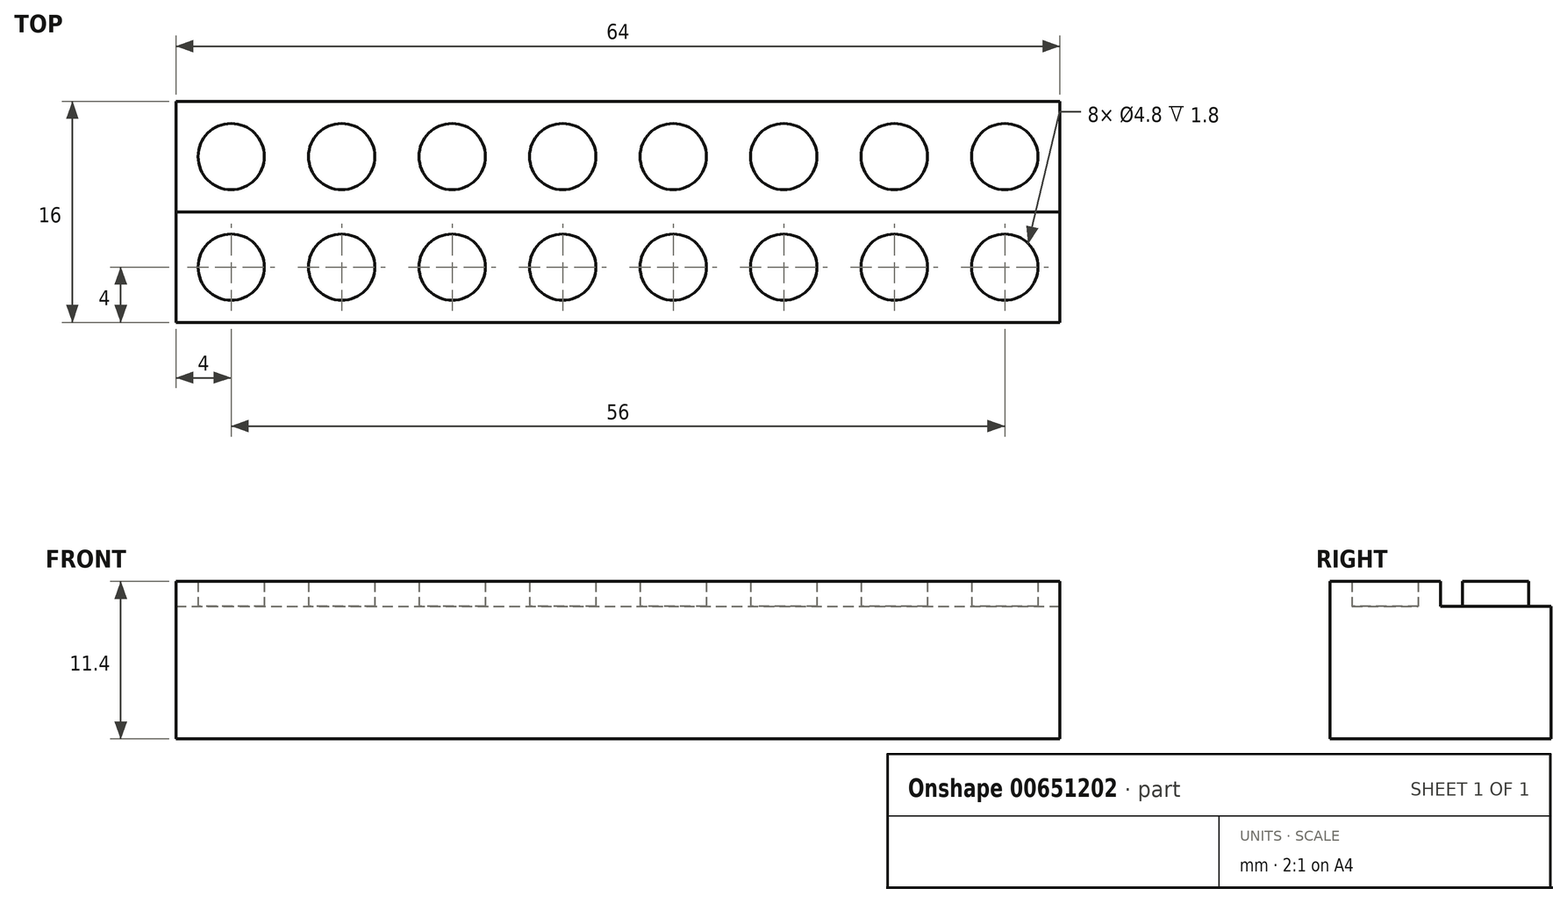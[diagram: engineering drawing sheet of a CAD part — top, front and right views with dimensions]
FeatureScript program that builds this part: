
annotation { "Feature Type Name" : "Feature", "Feature Type Description" : "" }
export const myFeature = defineFeature(function(context is Context, id is Id, definition is map)
    precondition{}
    {
        {
            var Q0;
            Q0=qCreatedBy(makeId("Top.planeOp"),FACE);
            var sketch = newSketch(context, id + "F0", { "sketchPlane" : qUnion([Q0])});
            skLineSegment(sketch, "E0.bottom", {"start": v(0, 0) * mm, "end": v(-64, 0) * mm});
            skLineSegment(sketch, "E0.top", {"start": v(0, 16) * mm, "end": v(-64, 16) * mm});
            skLineSegment(sketch, "E0.left", {"start": v(0, 0) * mm, "end": v(0, 16) * mm});
            skLineSegment(sketch, "E0.right", {"start": v(-64, 0) * mm, "end": v(-64, 16) * mm});
            skSolve(sketch);
        }
        {
            var Q0;
            Q0=makeQuery(id+"F0.imprint","IMPRINT",FACE,{"disambiguationData":[TD([[makeQuery(id+"F0.imprint","IMPRINT",EDGE,{"derivedFrom":sQuery(id+"F0.wireOp",EDGE,"E0.bottom")}),-1.0]])]});
            extrude(context, id + "F1", {"entities" : qUnion([Q0]), "depth" : 9.6 * mm, "offsetDistance" : 25.4 * mm});
        }
        {
            var Q0;
            Q0=makeQuery(id+"F1.opExtrude","CAP_FACE",FACE,{"disambiguationData":[OSD([sQuery(id+"F0.wireOp",EDGE,"E0.bottom"),sQuery(id+"F0.wireOp",EDGE,"E0.top"),sQuery(id+"F0.wireOp",EDGE,"E0.left"),sQuery(id+"F0.wireOp",EDGE,"E0.right")])],"isStart":false});
            var sketch = newSketch(context, id + "F2", { "sketchPlane" : qUnion([Q0])});
            skLineSegment(sketch, "E1", {"start": v(-64, 8) * mm, "end": v(0, 8) * mm});
            skLineSegment(sketch, "E2", {"start": v(-32, 16) * mm, "end": v(-32, 0) * mm});
            skLineSegment(sketch, "E3", {"start": v(-56, 16) * mm, "end": v(-56, 0) * mm});
            skLineSegment(sketch, "E4", {"start": v(-48, 16) * mm, "end": v(-48, 0) * mm});
            skLineSegment(sketch, "E5", {"start": v(-40, 16) * mm, "end": v(-40, 0) * mm});
            skLineSegment(sketch, "E6", {"start": v(-24, 16) * mm, "end": v(-24, 0) * mm});
            skLineSegment(sketch, "E7", {"start": v(-16, 0) * mm, "end": v(-16, 16) * mm});
            skLineSegment(sketch, "E8", {"start": v(-8, 16) * mm, "end": v(-8, 0) * mm});
            skLineSegment(sketch, "E9", {"start": v(-64, 16) * mm, "end": v(-56, 8) * mm});
            skLineSegment(sketch, "E10", {"start": v(-56, 8) * mm, "end": v(-48, 16) * mm});
            skLineSegment(sketch, "E11", {"start": v(-48, 16) * mm, "end": v(-40, 8) * mm});
            skLineSegment(sketch, "E12", {"start": v(-40, 8) * mm, "end": v(-32, 16) * mm});
            skLineSegment(sketch, "E13", {"start": v(-32, 16) * mm, "end": v(-24, 8) * mm});
            skLineSegment(sketch, "E14", {"start": v(-24, 8) * mm, "end": v(-16, 16) * mm});
            skLineSegment(sketch, "E15", {"start": v(-16, 16) * mm, "end": v(-8, 8) * mm});
            skLineSegment(sketch, "E16", {"start": v(-8, 8) * mm, "end": v(0, 16) * mm});
            skCircle(sketch, "E17", {"center": v(-60, 12) * mm, "radius": 2.4 * mm});
            skCircle(sketch, "E18", {"center": v(-52, 12) * mm, "radius": 2.4 * mm});
            skCircle(sketch, "E19", {"center": v(-44, 12) * mm, "radius": 2.4 * mm});
            skCircle(sketch, "E20", {"center": v(-36, 12) * mm, "radius": 2.4 * mm});
            skCircle(sketch, "E21", {"center": v(-28, 12) * mm, "radius": 2.4 * mm});
            skCircle(sketch, "E22", {"center": v(-20, 12) * mm, "radius": 2.4 * mm});
            skCircle(sketch, "E23", {"center": v(-12, 12) * mm, "radius": 2.4 * mm});
            skCircle(sketch, "E24", {"center": v(-4, 12) * mm, "radius": 2.4 * mm});
            skCircle(sketch, "E25.MirrorC", {"center": v(-60, 4) * mm, "radius": 2.4 * mm});
            skCircle(sketch, "E26.MirrorC", {"center": v(-52, 4) * mm, "radius": 2.4 * mm});
            skCircle(sketch, "E27.MirrorC", {"center": v(-44, 4) * mm, "radius": 2.4 * mm});
            skCircle(sketch, "E28.MirrorC", {"center": v(-36, 4) * mm, "radius": 2.4 * mm});
            skCircle(sketch, "E29.MirrorC", {"center": v(-28, 4) * mm, "radius": 2.4 * mm});
            skCircle(sketch, "E30.MirrorC", {"center": v(-20, 4) * mm, "radius": 2.4 * mm});
            skCircle(sketch, "E31.MirrorC", {"center": v(-12, 4) * mm, "radius": 2.4 * mm});
            skCircle(sketch, "E32.MirrorC", {"center": v(-4, 4) * mm, "radius": 2.4 * mm});
            skSolve(sketch);
        }
        {
            var Q0;
            Q0=makeQuery(id+"F2.imprint","IMPRINT",FACE,{"disambiguationData":[TD([[makeQuery(id+"F2.imprint","IMPRINT",EDGE,{"derivedFrom":sQuery(id+"F2.wireOp",EDGE,"E25.MirrorC")}),-1.0]])]});
            var Q1;
            {var subQ0=sQuery(id+"F2.wireOp",EDGE,"E17");var subQ1=sQuery(id+"F2.wireOp",EDGE,"E9");var subQ2=makeQuery(id+"F2.imprint","INTERSECT",VERTEX,{"disambiguationData":[OD(0.0)],"derivedFrom":[subQ1,subQ0]});Q1=makeQuery(id+"F2.imprint","IMPRINT",FACE,{"disambiguationData":[TD([[makeQuery(id+"F2.imprint","IMPRINT",EDGE,{"disambiguationData":[TD([[subQ2,-1.0]])],"derivedFrom":subQ1}),-1.0]])]});}
            var Q2;
            {var subQ0=sQuery(id+"F2.wireOp",EDGE,"E17");var subQ1=sQuery(id+"F2.wireOp",EDGE,"E9");var subQ2=makeQuery(id+"F2.imprint","INTERSECT",VERTEX,{"disambiguationData":[OD(0.0)],"derivedFrom":[subQ1,subQ0]});Q2=makeQuery(id+"F2.imprint","IMPRINT",FACE,{"disambiguationData":[TD([[makeQuery(id+"F2.imprint","IMPRINT",EDGE,{"disambiguationData":[TD([[subQ2,-1.0]])],"derivedFrom":subQ1}),1.0]])]});}
            var Q3;
            {var subQ0=sQuery(id+"F2.wireOp",EDGE,"E18");var subQ1=sQuery(id+"F2.wireOp",EDGE,"E10");var subQ2=makeQuery(id+"F2.imprint","INTERSECT",VERTEX,{"disambiguationData":[OD(0.0)],"derivedFrom":[subQ1,subQ0]});Q3=makeQuery(id+"F2.imprint","IMPRINT",FACE,{"disambiguationData":[TD([[makeQuery(id+"F2.imprint","IMPRINT",EDGE,{"disambiguationData":[TD([[subQ2,-1.0]])],"derivedFrom":subQ1}),1.0]])]});}
            var Q4;
            {var subQ0=sQuery(id+"F2.wireOp",EDGE,"E18");var subQ1=sQuery(id+"F2.wireOp",EDGE,"E10");var subQ2=makeQuery(id+"F2.imprint","INTERSECT",VERTEX,{"disambiguationData":[OD(0.0)],"derivedFrom":[subQ1,subQ0]});Q4=makeQuery(id+"F2.imprint","IMPRINT",FACE,{"disambiguationData":[TD([[makeQuery(id+"F2.imprint","IMPRINT",EDGE,{"disambiguationData":[TD([[subQ2,-1.0]])],"derivedFrom":subQ1}),-1.0]])]});}
            var Q5;
            {var subQ0=sQuery(id+"F2.wireOp",EDGE,"E19");var subQ1=sQuery(id+"F2.wireOp",EDGE,"E11");var subQ2=makeQuery(id+"F2.imprint","INTERSECT",VERTEX,{"disambiguationData":[OD(0.0)],"derivedFrom":[subQ1,subQ0]});Q5=makeQuery(id+"F2.imprint","IMPRINT",FACE,{"disambiguationData":[TD([[makeQuery(id+"F2.imprint","IMPRINT",EDGE,{"disambiguationData":[TD([[subQ2,-1.0]])],"derivedFrom":subQ1}),-1.0]])]});}
            var Q6;
            {var subQ0=sQuery(id+"F2.wireOp",EDGE,"E19");var subQ1=sQuery(id+"F2.wireOp",EDGE,"E11");var subQ2=makeQuery(id+"F2.imprint","INTERSECT",VERTEX,{"disambiguationData":[OD(0.0)],"derivedFrom":[subQ1,subQ0]});Q6=makeQuery(id+"F2.imprint","IMPRINT",FACE,{"disambiguationData":[TD([[makeQuery(id+"F2.imprint","IMPRINT",EDGE,{"disambiguationData":[TD([[subQ2,-1.0]])],"derivedFrom":subQ1}),1.0]])]});}
            var Q7;
            {var subQ0=sQuery(id+"F2.wireOp",EDGE,"E20");var subQ1=sQuery(id+"F2.wireOp",EDGE,"E12");var subQ2=makeQuery(id+"F2.imprint","INTERSECT",VERTEX,{"disambiguationData":[OD(0.0)],"derivedFrom":[subQ1,subQ0]});Q7=makeQuery(id+"F2.imprint","IMPRINT",FACE,{"disambiguationData":[TD([[makeQuery(id+"F2.imprint","IMPRINT",EDGE,{"disambiguationData":[TD([[subQ2,-1.0]])],"derivedFrom":subQ1}),1.0]])]});}
            var Q8;
            {var subQ0=sQuery(id+"F2.wireOp",EDGE,"E20");var subQ1=sQuery(id+"F2.wireOp",EDGE,"E12");var subQ2=makeQuery(id+"F2.imprint","INTERSECT",VERTEX,{"disambiguationData":[OD(0.0)],"derivedFrom":[subQ1,subQ0]});Q8=makeQuery(id+"F2.imprint","IMPRINT",FACE,{"disambiguationData":[TD([[makeQuery(id+"F2.imprint","IMPRINT",EDGE,{"disambiguationData":[TD([[subQ2,-1.0]])],"derivedFrom":subQ1}),-1.0]])]});}
            var Q9;
            {var subQ0=sQuery(id+"F2.wireOp",EDGE,"E21");var subQ1=sQuery(id+"F2.wireOp",EDGE,"E13");var subQ2=makeQuery(id+"F2.imprint","INTERSECT",VERTEX,{"disambiguationData":[OD(0.0)],"derivedFrom":[subQ1,subQ0]});Q9=makeQuery(id+"F2.imprint","IMPRINT",FACE,{"disambiguationData":[TD([[makeQuery(id+"F2.imprint","IMPRINT",EDGE,{"disambiguationData":[TD([[subQ2,-1.0]])],"derivedFrom":subQ1}),-1.0]])]});}
            var Q10;
            {var subQ0=sQuery(id+"F2.wireOp",EDGE,"E21");var subQ1=sQuery(id+"F2.wireOp",EDGE,"E13");var subQ2=makeQuery(id+"F2.imprint","INTERSECT",VERTEX,{"disambiguationData":[OD(0.0)],"derivedFrom":[subQ1,subQ0]});Q10=makeQuery(id+"F2.imprint","IMPRINT",FACE,{"disambiguationData":[TD([[makeQuery(id+"F2.imprint","IMPRINT",EDGE,{"disambiguationData":[TD([[subQ2,-1.0]])],"derivedFrom":subQ1}),1.0]])]});}
            var Q11;
            {var subQ0=sQuery(id+"F2.wireOp",EDGE,"E22");var subQ1=sQuery(id+"F2.wireOp",EDGE,"E14");var subQ2=makeQuery(id+"F2.imprint","INTERSECT",VERTEX,{"disambiguationData":[OD(0.0)],"derivedFrom":[subQ1,subQ0]});Q11=makeQuery(id+"F2.imprint","IMPRINT",FACE,{"disambiguationData":[TD([[makeQuery(id+"F2.imprint","IMPRINT",EDGE,{"disambiguationData":[TD([[subQ2,-1.0]])],"derivedFrom":subQ1}),1.0]])]});}
            var Q12;
            {var subQ0=sQuery(id+"F2.wireOp",EDGE,"E22");var subQ1=sQuery(id+"F2.wireOp",EDGE,"E14");var subQ2=makeQuery(id+"F2.imprint","INTERSECT",VERTEX,{"disambiguationData":[OD(0.0)],"derivedFrom":[subQ1,subQ0]});Q12=makeQuery(id+"F2.imprint","IMPRINT",FACE,{"disambiguationData":[TD([[makeQuery(id+"F2.imprint","IMPRINT",EDGE,{"disambiguationData":[TD([[subQ2,-1.0]])],"derivedFrom":subQ1}),-1.0]])]});}
            var Q13;
            {var subQ0=sQuery(id+"F2.wireOp",EDGE,"E23");var subQ1=sQuery(id+"F2.wireOp",EDGE,"E15");var subQ2=makeQuery(id+"F2.imprint","INTERSECT",VERTEX,{"disambiguationData":[OD(0.0)],"derivedFrom":[subQ1,subQ0]});Q13=makeQuery(id+"F2.imprint","IMPRINT",FACE,{"disambiguationData":[TD([[makeQuery(id+"F2.imprint","IMPRINT",EDGE,{"disambiguationData":[TD([[subQ2,-1.0]])],"derivedFrom":subQ1}),-1.0]])]});}
            var Q14;
            {var subQ0=sQuery(id+"F2.wireOp",EDGE,"E23");var subQ1=sQuery(id+"F2.wireOp",EDGE,"E15");var subQ2=makeQuery(id+"F2.imprint","INTERSECT",VERTEX,{"disambiguationData":[OD(0.0)],"derivedFrom":[subQ1,subQ0]});Q14=makeQuery(id+"F2.imprint","IMPRINT",FACE,{"disambiguationData":[TD([[makeQuery(id+"F2.imprint","IMPRINT",EDGE,{"disambiguationData":[TD([[subQ2,-1.0]])],"derivedFrom":subQ1}),1.0]])]});}
            var Q15;
            {var subQ0=sQuery(id+"F2.wireOp",EDGE,"E24");var subQ1=sQuery(id+"F2.wireOp",EDGE,"E16");var subQ2=makeQuery(id+"F2.imprint","INTERSECT",VERTEX,{"disambiguationData":[OD(0.0)],"derivedFrom":[subQ1,subQ0]});Q15=makeQuery(id+"F2.imprint","IMPRINT",FACE,{"disambiguationData":[TD([[makeQuery(id+"F2.imprint","IMPRINT",EDGE,{"disambiguationData":[TD([[subQ2,-1.0]])],"derivedFrom":subQ1}),1.0]])]});}
            var Q16;
            {var subQ0=sQuery(id+"F2.wireOp",EDGE,"E24");var subQ1=sQuery(id+"F2.wireOp",EDGE,"E16");var subQ2=makeQuery(id+"F2.imprint","INTERSECT",VERTEX,{"disambiguationData":[OD(0.0)],"derivedFrom":[subQ1,subQ0]});Q16=makeQuery(id+"F2.imprint","IMPRINT",FACE,{"disambiguationData":[TD([[makeQuery(id+"F2.imprint","IMPRINT",EDGE,{"disambiguationData":[TD([[subQ2,-1.0]])],"derivedFrom":subQ1}),-1.0]])]});}
            var Q17;
            Q17=makeQuery(id+"F2.imprint","IMPRINT",FACE,{"disambiguationData":[TD([[makeQuery(id+"F2.imprint","IMPRINT",EDGE,{"derivedFrom":sQuery(id+"F2.wireOp",EDGE,"E32.MirrorC")}),-1.0]])]});
            var Q18;
            Q18=makeQuery(id+"F2.imprint","IMPRINT",FACE,{"disambiguationData":[TD([[makeQuery(id+"F2.imprint","IMPRINT",EDGE,{"derivedFrom":sQuery(id+"F2.wireOp",EDGE,"E31.MirrorC")}),-1.0]])]});
            var Q19;
            Q19=makeQuery(id+"F2.imprint","IMPRINT",FACE,{"disambiguationData":[TD([[makeQuery(id+"F2.imprint","IMPRINT",EDGE,{"derivedFrom":sQuery(id+"F2.wireOp",EDGE,"E30.MirrorC")}),-1.0]])]});
            var Q20;
            Q20=makeQuery(id+"F2.imprint","IMPRINT",FACE,{"disambiguationData":[TD([[makeQuery(id+"F2.imprint","IMPRINT",EDGE,{"derivedFrom":sQuery(id+"F2.wireOp",EDGE,"E29.MirrorC")}),-1.0]])]});
            var Q21;
            Q21=makeQuery(id+"F2.imprint","IMPRINT",FACE,{"disambiguationData":[TD([[makeQuery(id+"F2.imprint","IMPRINT",EDGE,{"derivedFrom":sQuery(id+"F2.wireOp",EDGE,"E28.MirrorC")}),-1.0]])]});
            var Q22;
            Q22=makeQuery(id+"F2.imprint","IMPRINT",FACE,{"disambiguationData":[TD([[makeQuery(id+"F2.imprint","IMPRINT",EDGE,{"derivedFrom":sQuery(id+"F2.wireOp",EDGE,"E27.MirrorC")}),-1.0]])]});
            var Q23;
            Q23=makeQuery(id+"F2.imprint","IMPRINT",FACE,{"disambiguationData":[TD([[makeQuery(id+"F2.imprint","IMPRINT",EDGE,{"derivedFrom":sQuery(id+"F2.wireOp",EDGE,"E26.MirrorC")}),-1.0]])]});
            extrude(context, id + "F3", {"entities" : qUnion([Q0, Q1, Q2, Q3, Q4, Q5, Q6, Q7, Q8, Q9, Q10, Q11, Q12, Q13, Q14, Q15, Q16, Q17, Q18, Q19, Q20, Q21, Q22, Q23]), "operationType" : NewBodyOperationType.ADD, "depth" : 1.8 * mm, "offsetDistance" : 25.4 * mm});
        }
    });
